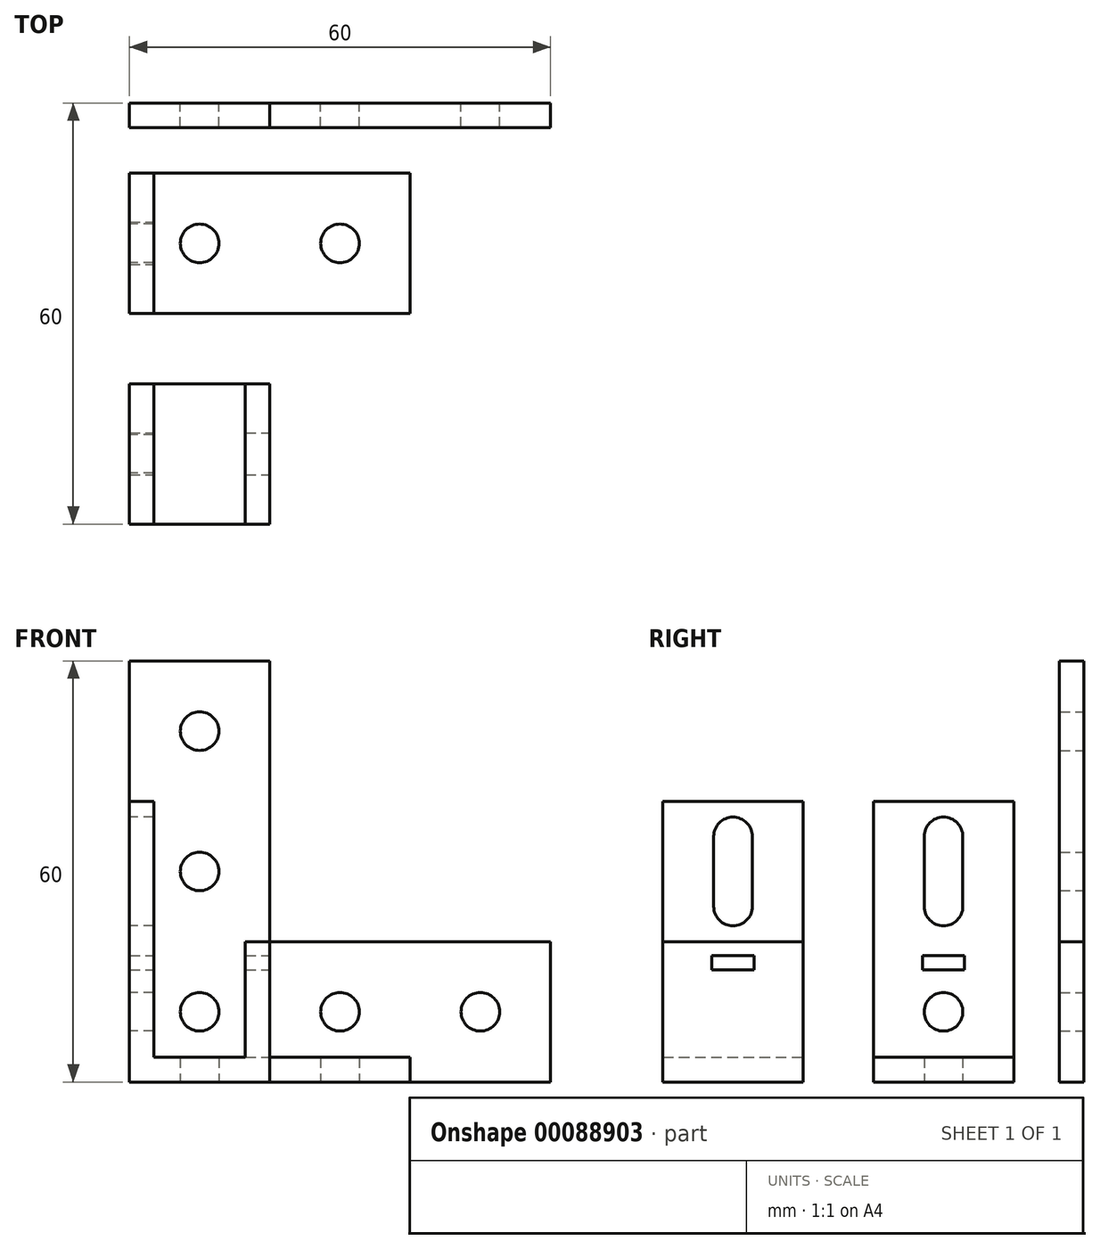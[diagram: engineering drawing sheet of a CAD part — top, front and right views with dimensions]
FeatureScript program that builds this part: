
annotation { "Feature Type Name" : "Feature", "Feature Type Description" : "" }
export const myFeature = defineFeature(function(context is Context, id is Id, definition is map)
    precondition{}
    {
        {
            var Q0;
            Q0=qCreatedBy(makeId("Front.planeOp"),FACE);
            var sketch = newSketch(context, id + "F0", { "sketchPlane" : qUnion([Q0])});
            skLineSegment(sketch, "E0.bottom", {"start": v(0, 0) * mm, "end": v(20, 0) * mm});
            skLineSegment(sketch, "E0.top", {"start": v(0, 60) * mm, "end": v(20, 60) * mm});
            skLineSegment(sketch, "E0.left", {"start": v(0, 0) * mm, "end": v(0, 60) * mm});
            skLineSegment(sketch, "E0.right", {"start": v(20, 20) * mm, "end": v(20, 60) * mm});
            skLineSegment(sketch, "E1.bottom", {"start": v(0, 0) * mm, "end": v(60, 0) * mm});
            skLineSegment(sketch, "E1.top", {"start": v(20, 20) * mm, "end": v(60, 20) * mm});
            skLineSegment(sketch, "E1.left", {"start": v(0, 0) * mm, "end": v(0, 20) * mm});
            skLineSegment(sketch, "E1.right", {"start": v(60, 0) * mm, "end": v(60, 20) * mm});
            skLineSegment(sketch, "E2", {"start": v(-33.76, 10) * mm, "end": v(70.27, 10) * mm, "construction": true});
            skLineSegment(sketch, "E3", {"start": v(10, 68.63) * mm, "end": v(10, -8.63) * mm, "construction": true});
            skPoint(sketch, "E3.endSnap0", {"position": v(10, 0) * mm});
            skCircle(sketch, "E4", {"center": v(10, 50) * mm, "radius": 2.75 * mm});
            skCircle(sketch, "E5", {"center": v(10, 30) * mm, "radius": 2.75 * mm});
            skCircle(sketch, "E6", {"center": v(30, 10) * mm, "radius": 2.75 * mm});
            skCircle(sketch, "E7", {"center": v(50, 10) * mm, "radius": 2.75 * mm});
            skLineSegment(sketch, "E8", {"start": v(-11.76, 40) * mm, "end": v(29.77, 40) * mm, "construction": true});
            skLineSegment(sketch, "E9", {"start": v(40, 30.44) * mm, "end": v(40, -9.65) * mm, "construction": true});
            skCircle(sketch, "E10", {"center": v(10, 10) * mm, "radius": 2.75 * mm});
            skSolve(sketch);
        }
        {
            var Q0;
            Q0 = qSketchRegion(id + "F0", true);
            extrude(context, id + "F1", {"entities" : qUnion([Q0]), "depth" : 3.5 * mm});
        }
        {
            var Q0;
            Q0=qCreatedBy(makeId("Front.planeOp"),FACE);
            var sketch = newSketch(context, id + "F2", { "sketchPlane" : qUnion([Q0])});
            skLineSegment(sketch, "E11.bottom", {"start": v(0, 0) * mm, "end": v(3.5, 0) * mm});
            skLineSegment(sketch, "E11.top", {"start": v(0, 40) * mm, "end": v(3.5, 40) * mm});
            skLineSegment(sketch, "E11.left", {"start": v(0, 0) * mm, "end": v(0, 40) * mm});
            skLineSegment(sketch, "E11.right", {"start": v(3.5, 3.5) * mm, "end": v(3.5, 40) * mm});
            skLineSegment(sketch, "E12.bottom", {"start": v(0, 0) * mm, "end": v(40, 0) * mm});
            skLineSegment(sketch, "E12.top", {"start": v(3.5, 3.5) * mm, "end": v(40, 3.5) * mm});
            skLineSegment(sketch, "E12.left", {"start": v(0, 0) * mm, "end": v(0, 3.5) * mm});
            skLineSegment(sketch, "E12.right", {"start": v(40, 0) * mm, "end": v(40, 3.5) * mm});
            skSolve(sketch);
        }
        {
            var Q0;
            Q0 = qSketchRegion(id + "F2", true);
            extrude(context, id + "F3", {"entities" : qUnion([Q0]), "depth" : 20 * mm});
        }
        {
            var Q0;
            Q0=makeQuery(id+"F3.opExtrude","SWEPT_FACE",FACE,{"disambiguationData":[OSD([sQuery(id+"F2.wireOp",EDGE,"E11.left"),sQuery(id+"F2.wireOp",EDGE,"E12.left")])]});
            var sketch = newSketch(context, id + "F4", { "sketchPlane" : qUnion([Q0])});
            skLineSegment(sketch, "E13", {"start": v(10, 52.92) * mm, "end": v(10, -9.36) * mm, "construction": true});
            skLineSegment(sketch, "E14", {"start": v(-18.85, 20) * mm, "end": v(44.42, 20) * mm, "construction": true});
            skCircle(sketch, "E15", {"center": v(10, 30) * mm, "radius": 2.75 * mm});
            skCircle(sketch, "E16.MirrorC", {"center": v(10, 10) * mm, "radius": 2.75 * mm});
            skSolve(sketch);
        }
        {
            var Q0;
            Q0 = qSketchRegion(id + "F4", true);
            extrude(context, id + "F5", {"entities" : qUnion([Q0]), "operationType" : NewBodyOperationType.REMOVE, "endBound" : BoundingType.UP_TO_NEXT, "oppositeDirection" : true, "depth" : 25 * mm});
        }
        {
            var Q0;
            Q0=makeQuery(id+"F3.opExtrude","SWEPT_FACE",FACE,{"disambiguationData":[OSD([sQuery(id+"F2.wireOp",EDGE,"E12.bottom")])]});
            var sketch = newSketch(context, id + "F6", { "sketchPlane" : qUnion([Q0])});
            skLineSegment(sketch, "E17", {"start": v(20, -18.75) * mm, "end": v(20, 29.68) * mm, "construction": true});
            skLineSegment(sketch, "E18", {"start": v(-6.06, 10) * mm, "end": v(51, 10) * mm, "construction": true});
            skCircle(sketch, "E19", {"center": v(10, 10) * mm, "radius": 2.75 * mm});
            skCircle(sketch, "E20.MirrorC", {"center": v(30, 10) * mm, "radius": 2.75 * mm});
            skSolve(sketch);
        }
        {
            var Q0;
            Q0 = qSketchRegion(id + "F6", true);
            extrude(context, id + "F7", {"entities" : qUnion([Q0]), "operationType" : NewBodyOperationType.REMOVE, "endBound" : BoundingType.UP_TO_NEXT, "oppositeDirection" : true, "depth" : 25 * mm});
        }
        {
            var Q0;
            Q0=qCreatedBy(makeId("Front.planeOp"),FACE);
            var sketch = newSketch(context, id + "F8", { "sketchPlane" : qUnion([Q0])});
            skLineSegment(sketch, "E21.bottom", {"start": v(0, 0) * mm, "end": v(3.5, 0) * mm});
            skLineSegment(sketch, "E21.top", {"start": v(0, 40) * mm, "end": v(3.5, 40) * mm});
            skLineSegment(sketch, "E21.left", {"start": v(0, 0) * mm, "end": v(0, 40) * mm});
            skLineSegment(sketch, "E21.right", {"start": v(3.5, 3.5) * mm, "end": v(3.5, 40) * mm});
            skLineSegment(sketch, "E22.bottom", {"start": v(3.5, 0) * mm, "end": v(20, 0) * mm});
            skLineSegment(sketch, "E22.top", {"start": v(3.5, 3.5) * mm, "end": v(16.5, 3.5) * mm});
            skLineSegment(sketch, "E22.right", {"start": v(20, 0) * mm, "end": v(20, 3.5) * mm});
            skLineSegment(sketch, "E23.top", {"start": v(20, 20) * mm, "end": v(16.5, 20) * mm});
            skLineSegment(sketch, "E23.left", {"start": v(20, 3.5) * mm, "end": v(20, 20) * mm});
            skLineSegment(sketch, "E23.right", {"start": v(16.5, 3.5) * mm, "end": v(16.5, 20) * mm});
            skSolve(sketch);
        }
        {
            var Q0;
            Q0 = qSketchRegion(id + "F8", true);
            extrude(context, id + "F9", {"entities" : qUnion([Q0]), "depth" : 20 * mm});
        }
        {
            var Q0;
            Q0=makeQuery(id+"F9.opExtrude","SWEPT_FACE",FACE,{"disambiguationData":[OSD([sQuery(id+"F8.wireOp",EDGE,"E21.left")])]});
            var sketch = newSketch(context, id + "F10", { "sketchPlane" : qUnion([Q0])});
            skLineSegment(sketch, "E24", {"start": v(-18.8, 20) * mm, "end": v(53.68, 20) * mm, "construction": true});
            skLineSegment(sketch, "E25", {"start": v(10, 52.43) * mm, "end": v(10, -10.82) * mm, "construction": true});
            skArc(sketch, "E26", {"start": v(12.75, 35) * mm, "mid": v(10, 37.75) * mm, "end": v(7.25, 35) * mm});
            skLineSegment(sketch, "E27", {"start": v(-6.05, 30) * mm, "end": v(32.5, 30) * mm, "construction": true});
            skLineSegment(sketch, "E28", {"start": v(7.25, 35) * mm, "end": v(7.25, 30) * mm});
            skLineSegment(sketch, "E29", {"start": v(12.75, 35) * mm, "end": v(12.75, 30) * mm});
            skLineSegment(sketch, "E30.MirrorCS", {"start": v(12.75, 25) * mm, "end": v(12.75, 30) * mm});
            skLineSegment(sketch, "E31.MirrorCS", {"start": v(7.25, 25) * mm, "end": v(7.25, 30) * mm});
            skArc(sketch, "E32.MirrorCS", {"start": v(12.75, 25) * mm, "mid": v(10, 22.25) * mm, "end": v(7.25, 25) * mm});
            skSolve(sketch);
        }
        {
            var Q0;
            Q0 = qSketchRegion(id + "F10", true);
            extrude(context, id + "F11", {"entities" : qUnion([Q0]), "operationType" : NewBodyOperationType.REMOVE, "endBound" : BoundingType.UP_TO_NEXT, "oppositeDirection" : true, "depth" : 25 * mm});
        }
        {
            var Q0;
            Q0=makeQuery(id+"F9.opExtrude","SWEPT_FACE",FACE,{"disambiguationData":[OSD([sQuery(id+"F8.wireOp",EDGE,"E22.right"),sQuery(id+"F8.wireOp",EDGE,"E23.left")])]});
            var sketch = newSketch(context, id + "F12", { "sketchPlane" : qUnion([Q0])});
            skLineSegment(sketch, "E33", {"start": v(-10, -17.56) * mm, "end": v(-10, 28.95) * mm, "construction": true});
            skLineSegment(sketch, "E34.bottom", {"start": v(-13, 18) * mm, "end": v(-7, 18) * mm});
            skLineSegment(sketch, "E34.top", {"start": v(-13, 16) * mm, "end": v(-7, 16) * mm});
            skLineSegment(sketch, "E34.left", {"start": v(-13, 18) * mm, "end": v(-13, 16) * mm});
            skLineSegment(sketch, "E34.right", {"start": v(-7, 18) * mm, "end": v(-7, 16) * mm});
            skSolve(sketch);
        }
        {
            var Q0;
            Q0 = qSketchRegion(id + "F12", true);
            var Q1;
            Q1=makeQuery(id+"F9.opExtrude","SWEPT_FACE",FACE,{"disambiguationData":[OSD([sQuery(id+"F8.wireOp",EDGE,"E21.left")])]});
            extrude(context, id + "F13", {"entities" : qUnion([Q0]), "operationType" : NewBodyOperationType.REMOVE, "endBound" : BoundingType.UP_TO_SURFACE, "oppositeDirection" : true, "endBoundEntityFace" : qUnion([Q1]), "depth" : 25 * mm});
        }
        {
            var Q0;
            Q0=makeQuery(id+"F1.opExtrude","SWEPT_BODY",BODY,{"disambiguationData":[OSD([sQuery(id+"F0.wireOp",EDGE,"E0.top"),sQuery(id+"F0.wireOp",EDGE,"E0.left"),sQuery(id+"F0.wireOp",EDGE,"E0.right"),sQuery(id+"F0.wireOp",EDGE,"E1.bottom"),sQuery(id+"F0.wireOp",EDGE,"E1.top"),sQuery(id+"F0.wireOp",EDGE,"E1.left"),sQuery(id+"F0.wireOp",EDGE,"E1.right"),sQuery(id+"F0.wireOp",EDGE,"E4"),sQuery(id+"F0.wireOp",EDGE,"E5"),sQuery(id+"F0.wireOp",EDGE,"E6"),sQuery(id+"F0.wireOp",EDGE,"E7"),sQuery(id+"F0.wireOp",EDGE,"E10")])]});
            transform(context, id + "F14", {"entities" : qUnion([Q0]), "transformType" : TransformType.TRANSLATION_3D, "dx" : 0 * mm, "dy" : 10 * mm, "dz" : 0 * mm, "makeCopy" : false});
        }
        {
            var Q0;
            Q0=makeQuery(id+"F9.opExtrude","SWEPT_BODY",BODY,{"disambiguationData":[OSD([sQuery(id+"F8.wireOp",EDGE,"E21.bottom"),sQuery(id+"F8.wireOp",EDGE,"E21.top"),sQuery(id+"F8.wireOp",EDGE,"E21.left"),sQuery(id+"F8.wireOp",EDGE,"E21.right"),sQuery(id+"F8.wireOp",EDGE,"E22.bottom"),sQuery(id+"F8.wireOp",EDGE,"E22.top"),sQuery(id+"F8.wireOp",EDGE,"E22.right"),sQuery(id+"F8.wireOp",EDGE,"E23.top"),sQuery(id+"F8.wireOp",EDGE,"E23.left"),sQuery(id+"F8.wireOp",EDGE,"E23.right")])]});
            transform(context, id + "F15", {"entities" : qUnion([Q0]), "transformType" : TransformType.TRANSLATION_3D, "dx" : 0 * mm, "dy" : -30 * mm, "dz" : 0 * mm, "makeCopy" : false});
        }
    });
